# Revit family: Verbindungsplatte 2-Loch Lochung 13
name_source: partatom
category: HLS-Bauteile
revit_build: Autodesk Revit 2017 (Build: 20190507_1515(x64)
units: mm (PartAtom-declared; Revit-internal decimal feet)

## family parameters
Arbeitsebenenbasiert = Ja
Beim Laden mit Abzugskörper schneiden = Nein
Bemaßung runder Anschluss = Durchmesser verwenden
Gemeinsam genutzt = Ja
Immer vertikal = Nein
Raumberechnungspunkt = Nein
Teiletyp = Normal

## types (1)
- Verbindungsplatte 2-Loch Lochung 13
    Artikelnummer = 1660001413
    B = 40 mm  [stored 0.131234 ft]
    D = 13 mm
    EAN = 4250928449429
    Fabrikat = MEFA
    Firma = MEFA Befestigungs- und Montagesysteme GmbH
    Gewicht = 0.19 kg
    Gewicht pro Bauteil = 0.19 kg
    Kurztext1 = Verbindungsplatte 2-Loch
    Kurztext2 = Lochung 13 mm
    L = 120 mm  [stored 0.393701 ft]
    L1 = 75 mm
    Material = Stahl
    Vorgabe-Ansicht = 1219 mm

note: [stored X ft] marks values corroborated as IEEE doubles in the binary element streams (Revit-internal decimal feet)
